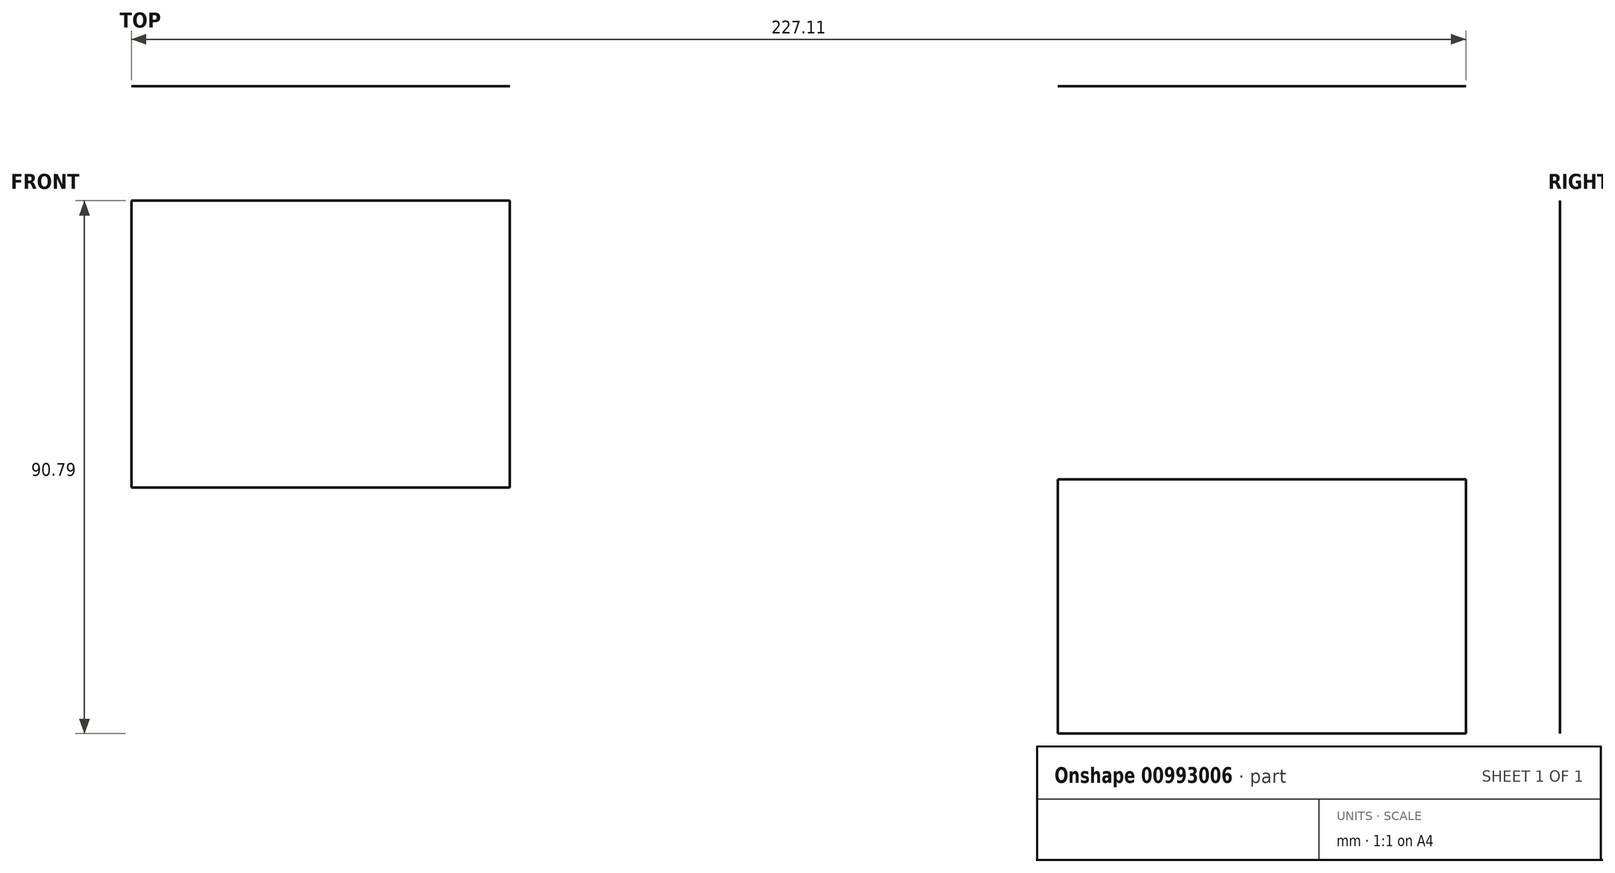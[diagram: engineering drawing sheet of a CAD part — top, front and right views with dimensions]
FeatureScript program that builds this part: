
annotation { "Feature Type Name" : "Feature", "Feature Type Description" : "" }
export const myFeature = defineFeature(function(context is Context, id is Id, definition is map)
    precondition{}
    {
        {
            var Q0;
            Q0=qCreatedBy(makeId("Front.planeOp"),FACE);
            var sketch = newSketch(context, id + "F0", { "sketchPlane" : qUnion([Q0])});
            skLineSegment(sketch, "E0.bottom", {"start": v(-172.16, 25.16) * mm, "end": v(-107.8, 25.16) * mm});
            skLineSegment(sketch, "E0.top", {"start": v(-172.16, -23.75) * mm, "end": v(-107.8, -23.75) * mm});
            skLineSegment(sketch, "E0.left", {"start": v(-172.16, 25.16) * mm, "end": v(-172.16, -23.75) * mm});
            skLineSegment(sketch, "E0.right", {"start": v(-107.8, 25.16) * mm, "end": v(-107.8, -23.75) * mm});
            skLineSegment(sketch, "E1.bottom", {"start": v(-14.48, -22.35) * mm, "end": v(54.95, -22.35) * mm});
            skLineSegment(sketch, "E1.top", {"start": v(-14.48, -65.63) * mm, "end": v(54.95, -65.63) * mm});
            skLineSegment(sketch, "E1.left", {"start": v(-14.48, -22.35) * mm, "end": v(-14.48, -65.63) * mm});
            skLineSegment(sketch, "E1.right", {"start": v(54.95, -22.35) * mm, "end": v(54.95, -65.63) * mm});
            skSolve(sketch);
        }
        {
            var Q0;
            Q0=sQuery(id+"F0.wireOp",EDGE,"E0.bottom");
            var Q1;
            Q1=sQuery(id+"F0.wireOp",EDGE,"E0.top");
            loft(context, id + "F1", {"bodyType" : ToolBodyType.SURFACE, "wireProfilesArray" : [{ "wireProfileEntities" : qUnion([Q0]) }, { "wireProfileEntities" : qUnion([Q1]) }]});
        }
        {
            var Q0;
            Q0=sQuery(id+"F0.wireOp",EDGE,"E1.bottom");
            var Q1;
            Q1=sQuery(id+"F0.wireOp",EDGE,"E1.top");
            loft(context, id + "F2", {"bodyType" : ToolBodyType.SURFACE, "wireProfilesArray" : [{ "wireProfileEntities" : qUnion([Q0]) }, { "wireProfileEntities" : qUnion([Q1]) }]});
        }
    });
